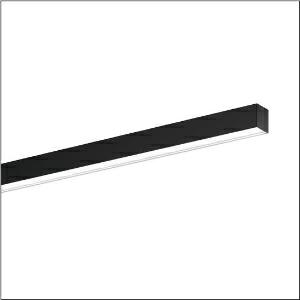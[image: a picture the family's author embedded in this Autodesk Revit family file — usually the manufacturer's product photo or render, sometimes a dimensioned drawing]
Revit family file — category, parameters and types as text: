
# Revit family: silica_r__21_51mx20dc45bb_0fdd
name_source: partatom
category: Lighting Fixtures
units: mm (PartAtom-declared; Revit-internal decimal feet)

## family parameters
Cut with Voids When Loaded = No
Host = Face
Light Source = No
Part Type = Normal
Room Calculation Point = No
Round Connector Dimension = Use Diameter
Shared = No

## types (1)
- --- (1 x LED, 6000 lm, 40.1 W, 4000K)
    Apparent Load = 40 VA
    CIE Flux Codes = 48 79 96 100 100
    Color Rendering = 80
    Color Temperature = 4000K
    Default Elevation = 1800 mm
    Description = Silica® 21, office luminaire, primary optical cover: cover, of PMMA, opal, light emission: direct distribution, primary light characteristic: symmetric, installation type: surface-mounted, LED, rated luminous flux: 6.000lm, luminous efficacy: 150lm/W, light colour: 840, colour temperature: 4000K, with terminal, 3+2-pole, max. 2.5mm², mains connection: 220..240V, AC, 50/60Hz, rated input power: 40.1W, luminaire housing, of aluminium, jet black (RAL 9005), length: 3.004mm, width: 53mm, height: 53mm, protection rating (complete): IP20, insulation class (complete): insulation class I (protective earthing), certification: CE, permissible operating ambient temperature: 0..+35°C, standard: EN 50419, packaging unit: 1 piece
    Height = 0 mm  [stored 0 ft]
    Lamp = 1 x LED
    Lamp Light Flux = 6000 lm
    Lamp Power = 40.1 W
    Lamp count = 1
    Length = 3004 mm
    Luminous efficacy = 150 lm/W
    Manufacturer = Siteco
    ModVariant = No
    Model = 51MX20DC45BB
    Mounting Place = Ceiling
    Mounting Type = Recessed
    Number of Poles = 1
    OnlyDefault = Yes
    Power Factor = 1
    Product Name = Silica® 21
    Product group = office luminaire | ceiling recessed
    ProductGroupID = 401
    Protection Class = Protection class I
    Protection Degree = IP 20
    RLX_Detail_Level = 1
    RLX_Emergency_Light_Flux = 0 lm
    RLX_Emergency_Type = 0
    RLX_Emergency_Type_DB = No
    RlxData = <blob elided: 28821 chars, md5=51bbea74>
    Socket = socket
    Standby Power = 0 W
    System Light Flux = 6000 lm
    System Power = 40 W
    Type Comments = factory setting: luminous flux: 100 % | dim-lin: 254 | 218 mA
    Type Image = l_1297760.jpg
    URL = http://relux.com
    VarID = @adj_047963
    Voltage = 0 V
    Weight = 0.00 kg
    Width = 53 mm

note: [stored X ft] marks values corroborated as IEEE doubles in the binary element streams (Revit-internal decimal feet)

## geometry (parser evidence)
native form markers: Blend x4, Sweep x9
no freeform markers — native parametric forms only
